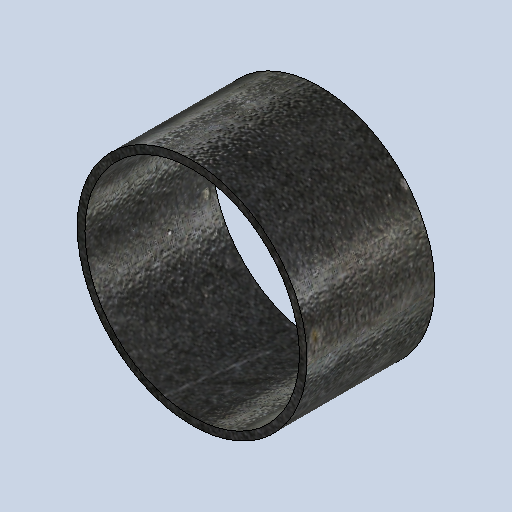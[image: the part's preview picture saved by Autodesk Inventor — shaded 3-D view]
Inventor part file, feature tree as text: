
AUTODESK INVENTOR PART (.ipt)
format: ipt  version: 2025 (Build 290162010, 162A)  size: 285,696 bytes
history: native  units: mm
features: extrude x1, sketch x1
ambient origin geometry x8: Origin, YZ Plane, XZ Plane, XY Plane, X Axis, Y Axis, Z Axis, Center Point
bodies: Solid1 (feature_tree)
feature tree (2):
  extrude  "Extrusion1"  Depth=50.0mm
  sketch  "Sketch1"  dims[d0=90.0mm d1=3.0mm d2=50.0mm d3=0.0mm]
